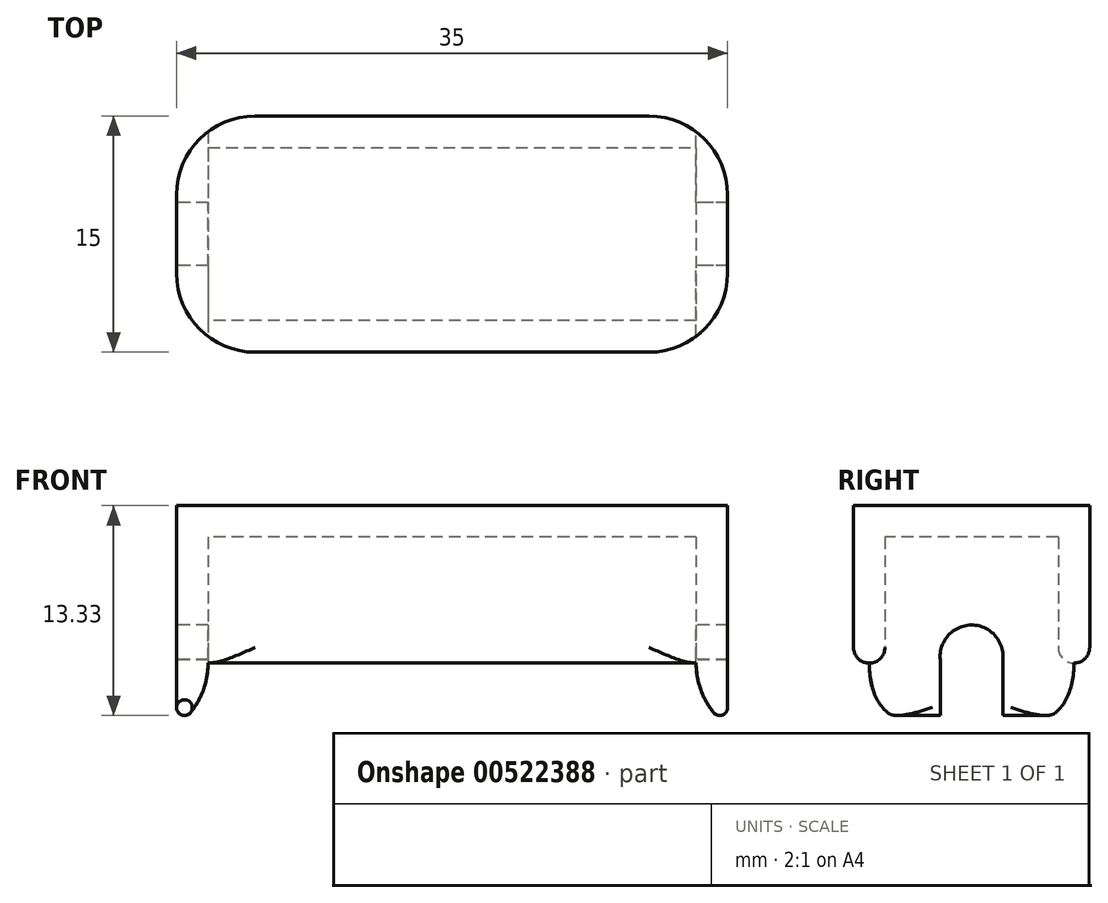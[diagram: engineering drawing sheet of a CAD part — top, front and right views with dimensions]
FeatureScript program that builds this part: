
annotation { "Feature Type Name" : "Feature", "Feature Type Description" : "" }
export const myFeature = defineFeature(function(context is Context, id is Id, definition is map)
    precondition{}
    {
        {
            var Q0;
            Q0=qCreatedBy(makeId("Top.planeOp"),FACE);
            var sketch = newSketch(context, id + "F0", { "sketchPlane" : qUnion([Q0])});
            skLineSegment(sketch, "E0", {"start": v(-35.23, 3.5) * mm, "end": v(-4.23, 3.5) * mm});
            skLineSegment(sketch, "E1", {"start": v(-4.23, 3.5) * mm, "end": v(-4.23, -7.5) * mm});
            skLineSegment(sketch, "E2", {"start": v(-4.23, -7.5) * mm, "end": v(-35.23, -7.5) * mm});
            skLineSegment(sketch, "E3", {"start": v(-35.23, -7.5) * mm, "end": v(-35.23, 3.5) * mm});
            skLineSegment(sketch, "E4.0", {"start": v(-2.23, -9.5) * mm, "end": v(-37.23, -9.5) * mm});
            skLineSegment(sketch, "E4.1", {"start": v(-2.23, 5.5) * mm, "end": v(-2.23, -9.5) * mm});
            skLineSegment(sketch, "E4.2", {"start": v(-37.23, 5.5) * mm, "end": v(-2.23, 5.5) * mm});
            skLineSegment(sketch, "E4.3", {"start": v(-37.23, -9.5) * mm, "end": v(-37.23, 5.5) * mm});
            skSolve(sketch);
        }
        {
            var Q0;
            Q0=makeQuery(id+"F0.imprint","IMPRINT",FACE,{"disambiguationData":[TD([[makeQuery(id+"F0.imprint","IMPRINT",EDGE,{"derivedFrom":sQuery(id+"F0.wireOp",EDGE,"E0")}),1.0]])]});
            extrude(context, id + "F1", {"entities" : qUnion([Q0]), "depth" : 12 * mm, "offsetDistance" : 25 * mm});
        }
        {
            var Q0;
            Q0=makeQuery(id+"F1.opExtrude","CAP_FACE",FACE,{"disambiguationData":[OSD([sQuery(id+"F0.wireOp",EDGE,"E0"),sQuery(id+"F0.wireOp",EDGE,"E1"),sQuery(id+"F0.wireOp",EDGE,"E2"),sQuery(id+"F0.wireOp",EDGE,"E3"),sQuery(id+"F0.wireOp",EDGE,"E4.0"),sQuery(id+"F0.wireOp",EDGE,"E4.1"),sQuery(id+"F0.wireOp",EDGE,"E4.2"),sQuery(id+"F0.wireOp",EDGE,"E4.3")])],"isStart":false});
            extrude(context, id + "F2", {"entities" : qUnion([Q0]), "operationType" : NewBodyOperationType.ADD, "depth" : 2 * mm, "offsetDistance" : 25 * mm});
        }
        {
            var Q0;
            {var subQ0=sQuery(id+"F0.wireOp",EDGE,"E3");Q0=makeQuery(id+"F2.boolean.opBoolean","MERGE",FACE,{"derivedFrom":[makeQuery(id+"F1.opExtrude","SWEPT_FACE",FACE,{"disambiguationData":[OSD([subQ0])]}),makeQuery(id+"F2.opExtrude","SWEPT_FACE",FACE,{"disambiguationData":[OSD([subQ0])]})]});}
            var sketch = newSketch(context, id + "F3", { "sketchPlane" : qUnion([Q0])});
            skLineSegment(sketch, "E5", {"start": v(3.5, 14) * mm, "end": v(3.5, 12) * mm});
            skLineSegment(sketch, "E6", {"start": v(3.5, 12) * mm, "end": v(-7.5, 12) * mm});
            skSolve(sketch);
        }
        {
            var Q0;
            Q0=makeQuery(id+"F3.imprint","IMPRINT",FACE,{"disambiguationData":[TD([[makeQuery(id+"F3.imprint","IMPRINT",EDGE,{"derivedFrom":sQuery(id+"F3.wireOp",EDGE,"E5")}),-1.0]])]});
            extrude(context, id + "F4", {"entities" : qUnion([Q0]), "operationType" : NewBodyOperationType.ADD, "endBound" : BoundingType.UP_TO_NEXT, "depth" : 25 * mm, "offsetDistance" : 25 * mm});
        }
        {
            var Q0;
            {var subQ0=sQuery(id+"F0.wireOp",EDGE,"E4.3");Q0=makeQuery(id+"F2.boolean.opBoolean","MERGE",FACE,{"derivedFrom":[makeQuery(id+"F1.opExtrude","SWEPT_FACE",FACE,{"disambiguationData":[OSD([subQ0])]}),makeQuery(id+"F2.opExtrude","SWEPT_FACE",FACE,{"disambiguationData":[OSD([subQ0])]})]});}
            var sketch = newSketch(context, id + "F5", { "sketchPlane" : qUnion([Q0])});
            skArc(sketch, "E7", {"start": v(3.98, 4.22) * mm, "mid": v(2, 6.42) * mm, "end": v(0, 4.25) * mm});
            skLineSegment(sketch, "E8", {"start": v(0, 4.25) * mm, "end": v(0, 0) * mm});
            skLineSegment(sketch, "E9", {"start": v(3.98, 4.22) * mm, "end": v(3.98, 0) * mm});
            skPoint(sketch, "E10.start.orphan", {"position": v(2, 0) * mm});
            skSolve(sketch);
        }
        {
            var Q0;
            Q0=makeQuery(id+"F5.imprint","IMPRINT",FACE,{"disambiguationData":[TD([[makeQuery(id+"F5.imprint","IMPRINT",EDGE,{"derivedFrom":sQuery(id+"F5.wireOp",EDGE,"E7")}),1.0]])]});
            extrude(context, id + "F6", {"entities" : qUnion([Q0]), "operationType" : NewBodyOperationType.REMOVE, "oppositeDirection" : true, "depth" : 45.6 * mm, "offsetDistance" : 25 * mm});
        }
        {
            var Q0;
            Q0=makeQuery(id+"F1.opExtrude","CAP_EDGE",EDGE,{"disambiguationData":[OSD([sQuery(id+"F0.wireOp",EDGE,"E0")])],"isStart":true});
            var Q1;
            Q1=makeQuery(id+"F4.opExtrude","SWEPT_EDGE",EDGE,{"disambiguationData":[OSD([sQuery(id+"F0.wireOp",EDGE,"E0"),sQuery(id+"F0.wireOp",EDGE,"E3"),sQuery(id+"F3.wireOp",EDGE,"E5"),sQuery(id+"F3.wireOp",EDGE,"E6")])]});
            var Q2;
            Q2=makeQuery(id+"F4.opExtrude","CAP_EDGE",EDGE,{"disambiguationData":[OSD([sQuery(id+"F3.wireOp",EDGE,"E6")])],"isStart":false});
            var Q3;
            Q3=makeQuery(id+"F4.opExtrude","SWEPT_EDGE",EDGE,{"disambiguationData":[OSD([sQuery(id+"F0.wireOp",EDGE,"E2"),sQuery(id+"F0.wireOp",EDGE,"E3"),sQuery(id+"F3.wireOp",EDGE,"E6")])]});
            var Q4;
            Q4=makeQuery(id+"F4.opExtrude","CAP_EDGE",EDGE,{"disambiguationData":[OSD([sQuery(id+"F3.wireOp",EDGE,"E6")])],"isStart":true});
            var Q5;
            Q5=makeQuery(id+"F1.opExtrude","CAP_EDGE",EDGE,{"disambiguationData":[OSD([sQuery(id+"F0.wireOp",EDGE,"E2")])],"isStart":true});
            var Q6;
            {var subQ0=sQuery(id+"F0.wireOp",EDGE,"E1");var subQ1=sQuery(id+"F0.wireOp",EDGE,"E2");Q6=makeQuery(id+"F6.boolean.opBoolean","SPLIT",EDGE,{"disambiguationData":[TD([makeQuery(id+"F1.opExtrude","SWEPT_FACE",FACE,{"disambiguationData":[OSD([subQ1])]})])],"derivedFrom":makeQuery(id+"F1.opExtrude","CAP_EDGE",EDGE,{"disambiguationData":[OSD([subQ0])],"isStart":true})});}
            var Q7;
            {var subQ0=sQuery(id+"F0.wireOp",EDGE,"E1");var subQ1=sQuery(id+"F0.wireOp",EDGE,"E0");Q7=makeQuery(id+"F6.boolean.opBoolean","SPLIT",EDGE,{"disambiguationData":[TD([makeQuery(id+"F1.opExtrude","SWEPT_FACE",FACE,{"disambiguationData":[OSD([subQ1])]})])],"derivedFrom":makeQuery(id+"F1.opExtrude","CAP_EDGE",EDGE,{"disambiguationData":[OSD([subQ0])],"isStart":true})});}
            var Q8;
            {var subQ0=sQuery(id+"F0.wireOp",EDGE,"E0");var subQ1=sQuery(id+"F0.wireOp",EDGE,"E3");Q8=makeQuery(id+"F6.boolean.opBoolean","SPLIT",EDGE,{"disambiguationData":[TD([makeQuery(id+"F1.opExtrude","SWEPT_FACE",FACE,{"disambiguationData":[OSD([subQ0])]})])],"derivedFrom":makeQuery(id+"F1.opExtrude","CAP_EDGE",EDGE,{"disambiguationData":[OSD([subQ1])],"isStart":true})});}
            var Q9;
            {var subQ0=sQuery(id+"F0.wireOp",EDGE,"E2");var subQ1=sQuery(id+"F0.wireOp",EDGE,"E3");Q9=makeQuery(id+"F6.boolean.opBoolean","SPLIT",EDGE,{"disambiguationData":[TD([makeQuery(id+"F1.opExtrude","SWEPT_FACE",FACE,{"disambiguationData":[OSD([subQ0])]})])],"derivedFrom":makeQuery(id+"F1.opExtrude","CAP_EDGE",EDGE,{"disambiguationData":[OSD([subQ1])],"isStart":true})});}
            fillet(context, id + "F7", {"entities" : qUnion([Q0, Q1, Q2, Q3, Q4, Q5, Q6, Q7, Q8, Q9]), "radius" : 5 * mm, "tangentPropagation" : true, "allowEdgeOverflow" : false});
        }
        {
            var Q0;
            {var subQ0=sQuery(id+"F0.wireOp",EDGE,"E4.3");var subQ1=sQuery(id+"F0.wireOp",EDGE,"E0");var subQ2=sQuery(id+"F0.wireOp",EDGE,"E3");Q0=makeQuery(id+"F7.opFillet","BLEND_EDGE",EDGE,{"blendedFrom":[makeQuery(id+"F6.boolean.opBoolean","SPLIT",EDGE,{"disambiguationData":[TD([makeQuery(id+"F1.opExtrude","SWEPT_FACE",FACE,{"disambiguationData":[OSD([subQ1])]})])],"derivedFrom":makeQuery(id+"F1.opExtrude","CAP_EDGE",EDGE,{"disambiguationData":[OSD([subQ2])],"isStart":true})}),makeQuery(id+"F2.boolean.opBoolean","MERGE",FACE,{"derivedFrom":[makeQuery(id+"F1.opExtrude","SWEPT_FACE",FACE,{"disambiguationData":[OSD([subQ0])]}),makeQuery(id+"F2.opExtrude","SWEPT_FACE",FACE,{"disambiguationData":[OSD([subQ0])]})]})],"blendedInto":[makeQuery(id+"F2.boolean.opBoolean","MERGE",FACE,{"derivedFrom":[makeQuery(id+"F1.opExtrude","SWEPT_FACE",FACE,{"disambiguationData":[OSD([subQ0])]}),makeQuery(id+"F2.opExtrude","SWEPT_FACE",FACE,{"disambiguationData":[OSD([subQ0])]})]})]});}
            var Q1;
            {var subQ0=sQuery(id+"F0.wireOp",EDGE,"E4.3");var subQ1=sQuery(id+"F0.wireOp",EDGE,"E2");var subQ2=sQuery(id+"F0.wireOp",EDGE,"E3");Q1=makeQuery(id+"F7.opFillet","BLEND_EDGE",EDGE,{"blendedFrom":[makeQuery(id+"F6.boolean.opBoolean","SPLIT",EDGE,{"disambiguationData":[TD([makeQuery(id+"F1.opExtrude","SWEPT_FACE",FACE,{"disambiguationData":[OSD([subQ1])]})])],"derivedFrom":makeQuery(id+"F1.opExtrude","CAP_EDGE",EDGE,{"disambiguationData":[OSD([subQ2])],"isStart":true})}),makeQuery(id+"F2.boolean.opBoolean","MERGE",FACE,{"derivedFrom":[makeQuery(id+"F1.opExtrude","SWEPT_FACE",FACE,{"disambiguationData":[OSD([subQ0])]}),makeQuery(id+"F2.opExtrude","SWEPT_FACE",FACE,{"disambiguationData":[OSD([subQ0])]})]})],"blendedInto":[makeQuery(id+"F2.boolean.opBoolean","MERGE",FACE,{"derivedFrom":[makeQuery(id+"F1.opExtrude","SWEPT_FACE",FACE,{"disambiguationData":[OSD([subQ0])]}),makeQuery(id+"F2.opExtrude","SWEPT_FACE",FACE,{"disambiguationData":[OSD([subQ0])]})]})]});}
            var Q2;
            {var subQ0=sQuery(id+"F0.wireOp",EDGE,"E4.1");var subQ1=sQuery(id+"F0.wireOp",EDGE,"E1");var subQ2=sQuery(id+"F0.wireOp",EDGE,"E2");Q2=makeQuery(id+"F7.opFillet","BLEND_EDGE",EDGE,{"blendedFrom":[makeQuery(id+"F6.boolean.opBoolean","SPLIT",EDGE,{"disambiguationData":[TD([makeQuery(id+"F1.opExtrude","SWEPT_FACE",FACE,{"disambiguationData":[OSD([subQ2])]})])],"derivedFrom":makeQuery(id+"F1.opExtrude","CAP_EDGE",EDGE,{"disambiguationData":[OSD([subQ1])],"isStart":true})}),makeQuery(id+"F2.boolean.opBoolean","MERGE",FACE,{"derivedFrom":[makeQuery(id+"F1.opExtrude","SWEPT_FACE",FACE,{"disambiguationData":[OSD([subQ0])]}),makeQuery(id+"F2.opExtrude","SWEPT_FACE",FACE,{"disambiguationData":[OSD([subQ0])]})]})],"blendedInto":[makeQuery(id+"F2.boolean.opBoolean","MERGE",FACE,{"derivedFrom":[makeQuery(id+"F1.opExtrude","SWEPT_FACE",FACE,{"disambiguationData":[OSD([subQ0])]}),makeQuery(id+"F2.opExtrude","SWEPT_FACE",FACE,{"disambiguationData":[OSD([subQ0])]})]})]});}
            var Q3;
            {var subQ0=sQuery(id+"F0.wireOp",EDGE,"E4.1");var subQ1=sQuery(id+"F0.wireOp",EDGE,"E1");var subQ2=sQuery(id+"F0.wireOp",EDGE,"E0");Q3=makeQuery(id+"F7.opFillet","BLEND_EDGE",EDGE,{"blendedFrom":[makeQuery(id+"F6.boolean.opBoolean","SPLIT",EDGE,{"disambiguationData":[TD([makeQuery(id+"F1.opExtrude","SWEPT_FACE",FACE,{"disambiguationData":[OSD([subQ2])]})])],"derivedFrom":makeQuery(id+"F1.opExtrude","CAP_EDGE",EDGE,{"disambiguationData":[OSD([subQ1])],"isStart":true})}),makeQuery(id+"F2.boolean.opBoolean","MERGE",FACE,{"derivedFrom":[makeQuery(id+"F1.opExtrude","SWEPT_FACE",FACE,{"disambiguationData":[OSD([subQ0])]}),makeQuery(id+"F2.opExtrude","SWEPT_FACE",FACE,{"disambiguationData":[OSD([subQ0])]})]})],"blendedInto":[makeQuery(id+"F2.boolean.opBoolean","MERGE",FACE,{"derivedFrom":[makeQuery(id+"F1.opExtrude","SWEPT_FACE",FACE,{"disambiguationData":[OSD([subQ0])]}),makeQuery(id+"F2.opExtrude","SWEPT_FACE",FACE,{"disambiguationData":[OSD([subQ0])]})]})]});}
            fillet(context, id + "F8", {"entities" : qUnion([Q0, Q1, Q2, Q3]), "radius" : .5 * mm, "tangentPropagation" : true, "allowEdgeOverflow" : false});
        }
        {
            var Q0;
            {var subQ0=sQuery(id+"F0.wireOp",EDGE,"E4.2");Q0=makeQuery(id+"F7.opFillet","BLEND_EDGE",EDGE,{"blendedFrom":[makeQuery(id+"F1.opExtrude","CAP_EDGE",EDGE,{"disambiguationData":[OSD([sQuery(id+"F0.wireOp",EDGE,"E0")])],"isStart":true}),makeQuery(id+"F2.boolean.opBoolean","MERGE",FACE,{"derivedFrom":[makeQuery(id+"F1.opExtrude","SWEPT_FACE",FACE,{"disambiguationData":[OSD([subQ0])]}),makeQuery(id+"F2.opExtrude","SWEPT_FACE",FACE,{"disambiguationData":[OSD([subQ0])]})]})],"blendedInto":[makeQuery(id+"F2.boolean.opBoolean","MERGE",FACE,{"derivedFrom":[makeQuery(id+"F1.opExtrude","SWEPT_FACE",FACE,{"disambiguationData":[OSD([subQ0])]}),makeQuery(id+"F2.opExtrude","SWEPT_FACE",FACE,{"disambiguationData":[OSD([subQ0])]})]})]});}
            var Q1;
            {var subQ0=sQuery(id+"F0.wireOp",EDGE,"E4.0");Q1=makeQuery(id+"F7.opFillet","BLEND_EDGE",EDGE,{"blendedFrom":[makeQuery(id+"F1.opExtrude","CAP_EDGE",EDGE,{"disambiguationData":[OSD([sQuery(id+"F0.wireOp",EDGE,"E2")])],"isStart":true}),makeQuery(id+"F2.boolean.opBoolean","MERGE",FACE,{"derivedFrom":[makeQuery(id+"F1.opExtrude","SWEPT_FACE",FACE,{"disambiguationData":[OSD([subQ0])]}),makeQuery(id+"F2.opExtrude","SWEPT_FACE",FACE,{"disambiguationData":[OSD([subQ0])]})]})],"blendedInto":[makeQuery(id+"F2.boolean.opBoolean","MERGE",FACE,{"derivedFrom":[makeQuery(id+"F1.opExtrude","SWEPT_FACE",FACE,{"disambiguationData":[OSD([subQ0])]}),makeQuery(id+"F2.opExtrude","SWEPT_FACE",FACE,{"disambiguationData":[OSD([subQ0])]})]})]});}
            fillet(context, id + "F9", {"entities" : qUnion([Q0, Q1]), "radius" : 1 * mm, "tangentPropagation" : true, "allowEdgeOverflow" : false});
        }
        {
            var Q0;
            {var subQ0=sQuery(id+"F0.wireOp",EDGE,"E4.3");var subQ1=sQuery(id+"F0.wireOp",EDGE,"E4.0");Q0=makeQuery(id+"F2.boolean.opBoolean","MERGE",EDGE,{"derivedFrom":[makeQuery(id+"F1.opExtrude","SWEPT_EDGE",EDGE,{"disambiguationData":[OSD([subQ1,subQ0])]}),makeQuery(id+"F2.opExtrude","SWEPT_EDGE",EDGE,{"disambiguationData":[OSD([subQ1,subQ0])]})]});}
            var Q1;
            {var subQ0=sQuery(id+"F0.wireOp",EDGE,"E4.3");var subQ1=sQuery(id+"F0.wireOp",EDGE,"E4.2");Q1=makeQuery(id+"F2.boolean.opBoolean","MERGE",EDGE,{"derivedFrom":[makeQuery(id+"F1.opExtrude","SWEPT_EDGE",EDGE,{"disambiguationData":[OSD([subQ1,subQ0])]}),makeQuery(id+"F2.opExtrude","SWEPT_EDGE",EDGE,{"disambiguationData":[OSD([subQ1,subQ0])]})]});}
            var Q2;
            {var subQ0=sQuery(id+"F0.wireOp",EDGE,"E4.2");var subQ1=sQuery(id+"F0.wireOp",EDGE,"E4.1");Q2=makeQuery(id+"F2.boolean.opBoolean","MERGE",EDGE,{"derivedFrom":[makeQuery(id+"F1.opExtrude","SWEPT_EDGE",EDGE,{"disambiguationData":[OSD([subQ1,subQ0])]}),makeQuery(id+"F2.opExtrude","SWEPT_EDGE",EDGE,{"disambiguationData":[OSD([subQ1,subQ0])]})]});}
            var Q3;
            {var subQ0=sQuery(id+"F0.wireOp",EDGE,"E4.1");var subQ1=sQuery(id+"F0.wireOp",EDGE,"E4.0");Q3=makeQuery(id+"F2.boolean.opBoolean","MERGE",EDGE,{"derivedFrom":[makeQuery(id+"F1.opExtrude","SWEPT_EDGE",EDGE,{"disambiguationData":[OSD([subQ1,subQ0])]}),makeQuery(id+"F2.opExtrude","SWEPT_EDGE",EDGE,{"disambiguationData":[OSD([subQ1,subQ0])]})]});}
            var Q4;
            {var subQ0=sQuery(id+"F3.wireOp",EDGE,"E6");Q4=makeQuery(id+"F7.opFillet","BLEND_EDGE",EDGE,{"blendedFrom":[makeQuery(id+"F4.opExtrude","SWEPT_EDGE",EDGE,{"disambiguationData":[OSD([sQuery(id+"F0.wireOp",EDGE,"E0"),sQuery(id+"F0.wireOp",EDGE,"E3"),sQuery(id+"F3.wireOp",EDGE,"E5"),subQ0])]}),makeQuery(id+"F4.opExtrude","SWEPT_FACE",FACE,{"disambiguationData":[OSD([subQ0])]})],"blendedInto":[makeQuery(id+"F4.opExtrude","SWEPT_FACE",FACE,{"disambiguationData":[OSD([subQ0])]})]});}
            var Q5;
            {var subQ0=sQuery(id+"F3.wireOp",EDGE,"E6");Q5=makeQuery(id+"F7.opFillet","BLEND_EDGE",EDGE,{"blendedFrom":[makeQuery(id+"F4.opExtrude","SWEPT_EDGE",EDGE,{"disambiguationData":[OSD([sQuery(id+"F0.wireOp",EDGE,"E2"),sQuery(id+"F0.wireOp",EDGE,"E3"),subQ0])]}),makeQuery(id+"F4.opExtrude","SWEPT_FACE",FACE,{"disambiguationData":[OSD([subQ0])]})],"blendedInto":[makeQuery(id+"F4.opExtrude","SWEPT_FACE",FACE,{"disambiguationData":[OSD([subQ0])]})]});}
            fillet(context, id + "F10", {"entities" : qUnion([Q0, Q1, Q2, Q3, Q4, Q5]), "radius" : 5 * mm, "tangentPropagation" : true, "allowEdgeOverflow" : false});
        }
    });
